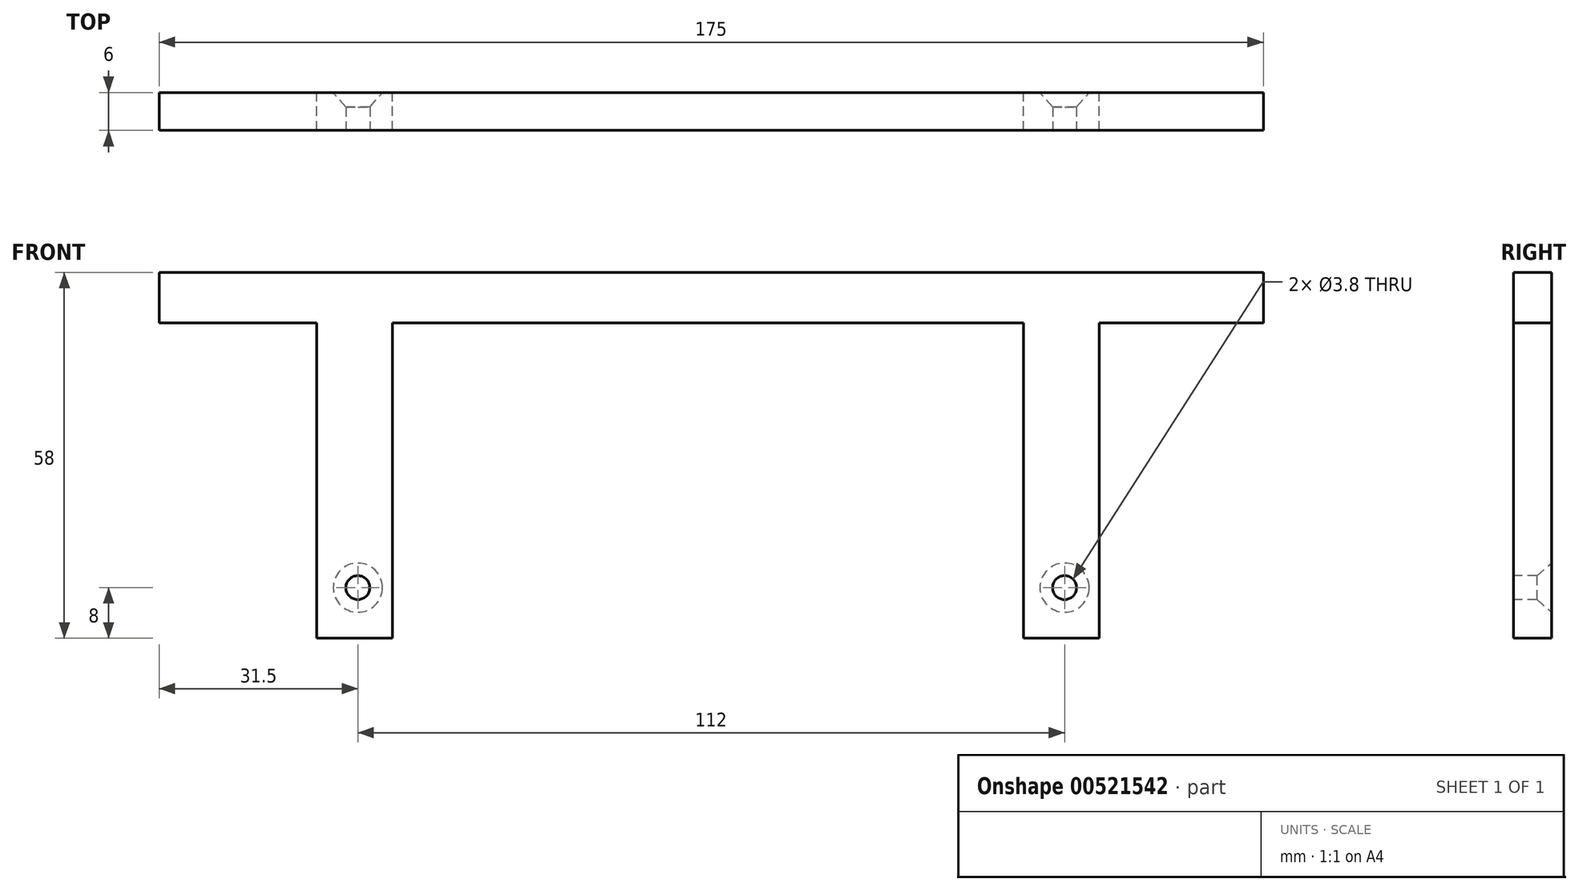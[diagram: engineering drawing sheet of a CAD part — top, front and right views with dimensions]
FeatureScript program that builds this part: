
annotation { "Feature Type Name" : "Feature", "Feature Type Description" : "" }
export const myFeature = defineFeature(function(context is Context, id is Id, definition is map)
    precondition{}
    {
        {
            var Q0;
            Q0=qCreatedBy(makeId("Front.planeOp"),FACE);
            var sketch = newSketch(context, id + "F0", { "sketchPlane" : qUnion([Q0])});
            skLineSegment(sketch, "E0", {"start": v(-87.5, 50) * mm, "end": v(-62.5, 50) * mm});
            skLineSegment(sketch, "E1", {"start": v(-62.5, 50) * mm, "end": v(-62.5, 0) * mm});
            skLineSegment(sketch, "E2", {"start": v(-62.5, 0) * mm, "end": v(-50.5, 0) * mm});
            skLineSegment(sketch, "E3", {"start": v(-50.5, 0) * mm, "end": v(-50.5, 50) * mm});
            skLineSegment(sketch, "E4", {"start": v(-50.5, 50) * mm, "end": v(49.5, 50) * mm});
            skLineSegment(sketch, "E5", {"start": v(49.5, 50) * mm, "end": v(49.5, 0) * mm});
            skLineSegment(sketch, "E6", {"start": v(49.5, 0) * mm, "end": v(61.5, 0) * mm});
            skLineSegment(sketch, "E7", {"start": v(61.5, 0) * mm, "end": v(61.5, 50) * mm});
            skLineSegment(sketch, "E8", {"start": v(61.5, 50) * mm, "end": v(87.5, 50) * mm});
            skLineSegment(sketch, "E9", {"start": v(87.5, 50) * mm, "end": v(87.5, 58) * mm});
            skLineSegment(sketch, "E10", {"start": v(87.5, 58) * mm, "end": v(-87.5, 58) * mm});
            skLineSegment(sketch, "E11", {"start": v(-87.5, 58) * mm, "end": v(-87.5, 50) * mm});
            skPoint(sketch, "E12", {"position": v(-56, 8) * mm});
            skPoint(sketch, "E13", {"position": v(56, 8) * mm});
            skSolve(sketch);
        }
        {
            var Q0;
            Q0=makeQuery(id+"F0.imprint","IMPRINT",FACE,{"disambiguationData":[TD([[makeQuery(id+"F0.imprint","IMPRINT",EDGE,{"derivedFrom":sQuery(id+"F0.wireOp",EDGE,"E0")}),1.0]])]});
            extrude(context, id + "F1", {"entities" : qUnion([Q0]), "depth" : 6 * mm, "offsetDistance" : 25 * mm});
        }
        {
            var Q0;
            Q0=sQuery(id+"F0.wireOp",VERTEX,"E12");
            var Q1;
            Q1=sQuery(id+"F0.wireOp",VERTEX,"E13");
            var Q2;
            Q2=makeQuery(id+"F1.opExtrude","SWEPT_BODY",BODY,{"disambiguationData":[OSD([sQuery(id+"F0.wireOp",EDGE,"E0"),sQuery(id+"F0.wireOp",EDGE,"E1"),sQuery(id+"F0.wireOp",EDGE,"E2"),sQuery(id+"F0.wireOp",EDGE,"E3"),sQuery(id+"F0.wireOp",EDGE,"E4"),sQuery(id+"F0.wireOp",EDGE,"E5"),sQuery(id+"F0.wireOp",EDGE,"E6"),sQuery(id+"F0.wireOp",EDGE,"E7"),sQuery(id+"F0.wireOp",EDGE,"E8"),sQuery(id+"F0.wireOp",EDGE,"E9"),sQuery(id+"F0.wireOp",EDGE,"E10"),sQuery(id+"F0.wireOp",EDGE,"E11")])]});
            hole(context, id + "F2", {"style" : HoleStyle.C_SINK, "endStyle" : HoleEndStyle.THROUGH, "oppositeDirection" : true, "standardTappedOrClearance" : lookupTablePath({ "standard" : "ANSI", "fit" : "Normal (ASME)", "size" : "#6", "type" : "Clearance" }), "standardBlindInLast" : lookupTablePath({ "fit" : "Free", "standard" : "ANSI", "size" : "#6", "type" : "Clearance" }), "holeDiameter" : 3.8 * mm, "cSinkDiameter" : 7.8 * mm, "cSinkAngle" : 82 * degree, "isTappedThrough" : true, "tappedDepth" : 12 * mm, "tapClearance" : 3, "locations" : qUnion([Q0, Q1]), "scope" : qUnion([Q2]), "startStyle" : HoleStartStyle.SKETCH});
        }
    });
